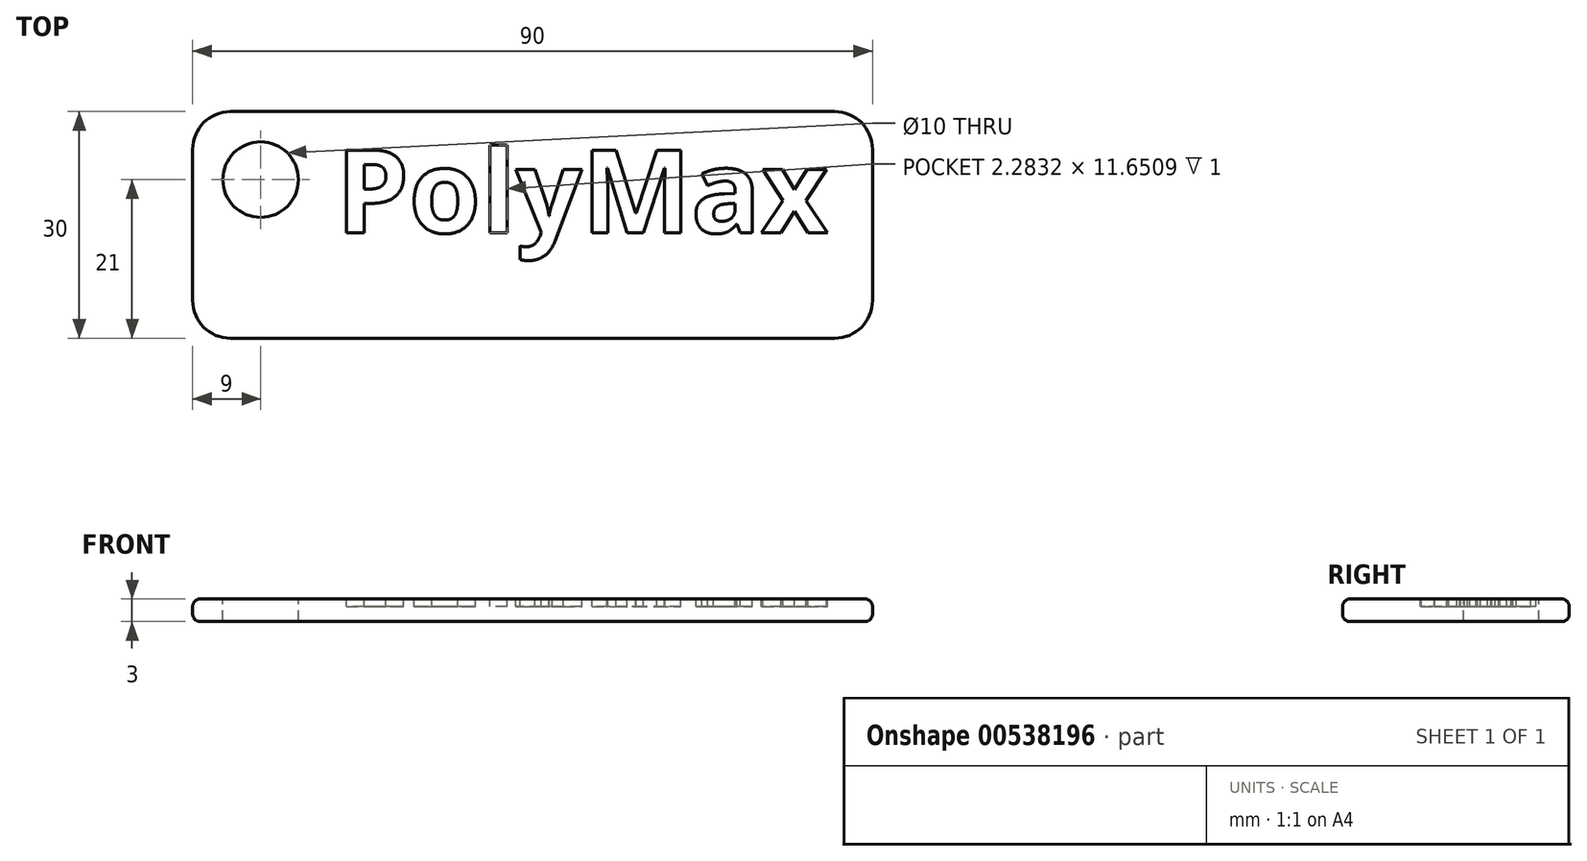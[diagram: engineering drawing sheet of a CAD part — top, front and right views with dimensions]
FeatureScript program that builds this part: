
annotation { "Feature Type Name" : "Feature", "Feature Type Description" : "" }
export const myFeature = defineFeature(function(context is Context, id is Id, definition is map)
    precondition{}
    {
        {
            var Q0;
            Q0=qCreatedBy(makeId("Top.planeOp"),FACE);
            var sketch = newSketch(context, id + "F0", { "sketchPlane" : qUnion([Q0])});
            skLineSegment(sketch, "E0.bottom", {"start": v(-45, 15) * mm, "end": v(45, 15) * mm});
            skLineSegment(sketch, "E0.top", {"start": v(-45, -15) * mm, "end": v(45, -15) * mm});
            skLineSegment(sketch, "E0.left", {"start": v(-45, 15) * mm, "end": v(-45, -15) * mm});
            skLineSegment(sketch, "E0.right", {"start": v(45, 15) * mm, "end": v(45, -15) * mm});
            skLineSegment(sketch, "E1", {"start": v(-45, 15) * mm, "end": v(45, -15) * mm, "construction": true});
            skSolve(sketch);
        }
        {
            var Q0;
            Q0=makeQuery(id+"F0.imprint","IMPRINT",FACE,{"disambiguationData":[TD([[makeQuery(id+"F0.imprint","IMPRINT",EDGE,{"derivedFrom":sQuery(id+"F0.wireOp",EDGE,"E0.bottom")}),-1.0]])]});
            extrude(context, id + "F1", {"entities" : qUnion([Q0]), "depth" : 3 * mm});
        }
        {
            var Q0;
            Q0=makeQuery(id+"F1.opExtrude","CAP_FACE",FACE,{"disambiguationData":[OSD([sQuery(id+"F0.wireOp",EDGE,"E0.bottom"),sQuery(id+"F0.wireOp",EDGE,"E0.top"),sQuery(id+"F0.wireOp",EDGE,"E0.left"),sQuery(id+"F0.wireOp",EDGE,"E0.right")])],"isStart":false});
            var Q1;
            Q1=makeQuery(id+"F1.opExtrude","CAP_FACE",FACE,{"disambiguationData":[OSD([sQuery(id+"F0.wireOp",EDGE,"E0.bottom"),sQuery(id+"F0.wireOp",EDGE,"E0.top"),sQuery(id+"F0.wireOp",EDGE,"E0.left"),sQuery(id+"F0.wireOp",EDGE,"E0.right")])],"isStart":true});
            fillet(context, id + "F2", {"entities" : qUnion([Q0, Q1]), "radius" : 1 * mm, "tangentPropagation" : true, "allowEdgeOverflow" : false});
        }
        {
            var Q0;
            Q0=makeQuery(id+"F1.opExtrude","SWEPT_EDGE",EDGE,{"disambiguationData":[OSD([sQuery(id+"F0.wireOp",EDGE,"E0.top"),sQuery(id+"F0.wireOp",EDGE,"E0.right")])]});
            var Q1;
            Q1=makeQuery(id+"F1.opExtrude","SWEPT_EDGE",EDGE,{"disambiguationData":[OSD([sQuery(id+"F0.wireOp",EDGE,"E0.bottom"),sQuery(id+"F0.wireOp",EDGE,"E0.right")])]});
            var Q2;
            Q2=makeQuery(id+"F1.opExtrude","SWEPT_EDGE",EDGE,{"disambiguationData":[OSD([sQuery(id+"F0.wireOp",EDGE,"E0.bottom"),sQuery(id+"F0.wireOp",EDGE,"E0.left")])]});
            var Q3;
            Q3=makeQuery(id+"F1.opExtrude","SWEPT_EDGE",EDGE,{"disambiguationData":[OSD([sQuery(id+"F0.wireOp",EDGE,"E0.top"),sQuery(id+"F0.wireOp",EDGE,"E0.left")])]});
            fillet(context, id + "F3", {"entities" : qUnion([Q0, Q1, Q2, Q3]), "radius" : 5 * mm, "tangentPropagation" : true, "allowEdgeOverflow" : false});
        }
        {
            var Q0;
            {var subQ0=sQuery(id+"F0.wireOp",EDGE,"E0.left");var subQ2=sQuery(id+"F0.wireOp",EDGE,"E0.bottom");var subQ4=sQuery(id+"F0.wireOp",EDGE,"E0.right");var subQ6=sQuery(id+"F0.wireOp",EDGE,"E0.top");Q0=makeQuery(id+"FmQCBBX3Ub0qneL_1.boolean.opBoolean","SPLIT",FACE,{"disambiguationData":[TD([makeQuery(id+"FmQCBBX3Ub0qneL_1.opExtrude","SWEPT_FACE",FACE,{"disambiguationData":[OSD([sQuery(id+"FOCoeRmDbjhRCuz_1.wireOp",EDGE,"4a1fb44a-e7be-4e23-9449-000d953c446c.sketch_text.stroke-0")])]})])],"derivedFrom":makeQuery(id+"F1.opExtrude","CAP_FACE",FACE,{"disambiguationData":[OSD([subQ2,subQ6,subQ0,subQ4])],"isStart":false})});}
            var sketch = newSketch(context, id + "F4", { "sketchPlane" : qUnion([Q0])});
            skCircle(sketch, "E2", {"center": v(-36, 6) * mm, "radius": 5 * mm});
            skSolve(sketch);
        }
        {
            var Q0;
            Q0=qSketchRegion(id+"F4",true);
            extrude(context, id + "F5", {"entities" : qUnion([Q0]), "operationType" : NewBodyOperationType.REMOVE, "oppositeDirection" : true, "depth" : 3 * mm});
        }
        {
            var Q0;
            Q0=makeQuery(id+"F1.opExtrude","CAP_FACE",FACE,{"disambiguationData":[OSD([sQuery(id+"F0.wireOp",EDGE,"E0.bottom"),sQuery(id+"F0.wireOp",EDGE,"E0.top"),sQuery(id+"F0.wireOp",EDGE,"E0.left"),sQuery(id+"F0.wireOp",EDGE,"E0.right")])],"isStart":false});
            var sketch = newSketch(context, id + "F6", { "sketchPlane" : qUnion([Q0])});
            skText(sketch, "E3", { "text": "PolyMax\n", "fontName": "OpenSans-Bold.ttf"});
            const initialGuessF6  = {"E3": [-0.026, -0.00104, 1, 0, 0.01104]};
            skSetInitialGuess(sketch, initialGuessF6);
            skSolve(sketch);
        }
        {
            var Q0;
            Q0=qSketchRegion(id+"F6",true);
            extrude(context, id + "F7", {"entities" : qUnion([Q0]), "operationType" : NewBodyOperationType.REMOVE, "oppositeDirection" : true, "depth" : 1 * mm});
        }
    });
